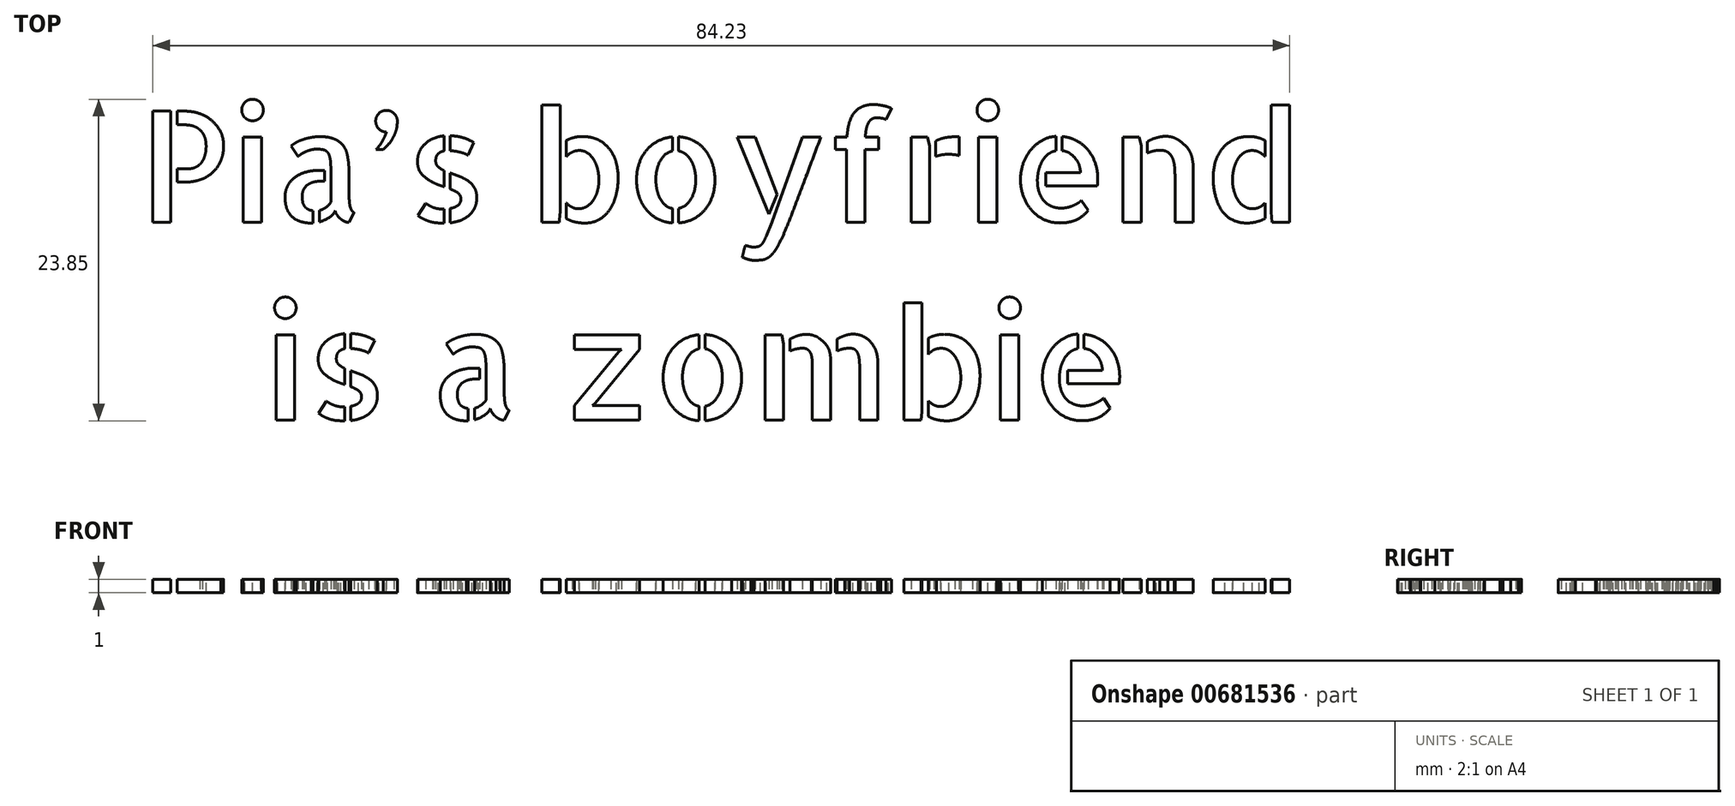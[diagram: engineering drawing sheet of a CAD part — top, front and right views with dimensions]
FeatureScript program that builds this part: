
annotation { "Feature Type Name" : "Feature", "Feature Type Description" : "" }
export const myFeature = defineFeature(function(context is Context, id is Id, definition is map)
    precondition{}
    {
        {
            var Q0;
            Q0=qCreatedBy(makeId("Top.planeOp"),FACE);
            var sketch = newSketch(context, id + "F0", { "sketchPlane" : qUnion([Q0])});
            skText(sketch, "E0", { "text": "Pia’s boyfriend\n   is a zombie", "fontName": "AllertaStencil-Regular.ttf"});
            const initialGuessF0  = {"E0": [-0.004, -0.00268, 1, 0, 0.00825]};
            skSetInitialGuess(sketch, initialGuessF0);
            skSolve(sketch);
        }
        {
            var Q0;
            Q0 = qSketchRegion(id + "F0", true);
            extrude(context, id + "F1", {"entities" : qUnion([Q0]), "depth" : 1 * mm, "offsetDistance" : 25 * mm});
        }
    });
